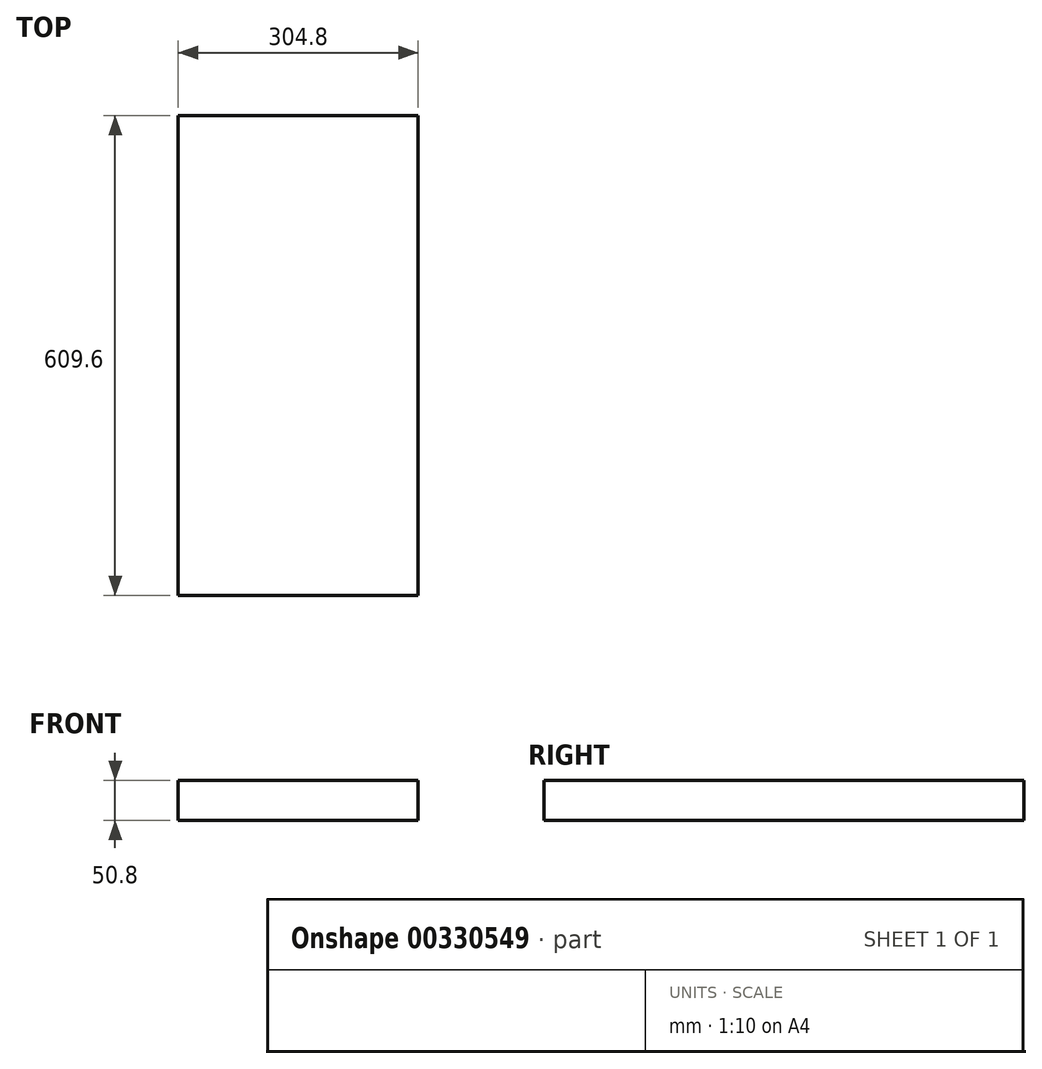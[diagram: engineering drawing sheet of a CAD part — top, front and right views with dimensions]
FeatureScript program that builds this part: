
annotation { "Feature Type Name" : "Feature", "Feature Type Description" : "" }
export const myFeature = defineFeature(function(context is Context, id is Id, definition is map)
    precondition{}
    {
        {
            var Q0;
            Q0=qCreatedBy(makeId("Top.planeOp"),FACE);
            var sketch = newSketch(context, id + "F0", { "sketchPlane" : qUnion([Q0])});
            skLineSegment(sketch, "E0.bottom", {"start": v(0, 0) * mm, "end": v(304.8, 0) * mm});
            skLineSegment(sketch, "E0.top", {"start": v(0, -609.6) * mm, "end": v(304.8, -609.6) * mm});
            skLineSegment(sketch, "E0.left", {"start": v(0, 0) * mm, "end": v(0, -609.6) * mm});
            skLineSegment(sketch, "E0.right", {"start": v(304.8, 0) * mm, "end": v(304.8, -609.6) * mm});
            skSolve(sketch);
        }
        {
            var Q0;
            Q0=makeQuery(id+"F0.imprint","IMPRINT",FACE,{"disambiguationData":[TD([[makeQuery(id+"F0.imprint","IMPRINT",EDGE,{"derivedFrom":sQuery(id+"F0.wireOp",EDGE,"E0.bottom")}),-1.0]])]});
            extrude(context, id + "F1", {"entities" : qUnion([Q0]), "depth" : 50.8 * mm});
        }
    });
